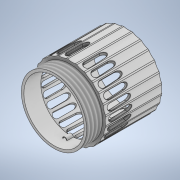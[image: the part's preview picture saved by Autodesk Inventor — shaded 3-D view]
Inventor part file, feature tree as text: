
AUTODESK INVENTOR PART (.ipt)
format: ipt  version: 2020.2 (Build 242310000, 310)  size: 1,843,200 bytes
history: native  units: mm
features: plane x14, sketch x11, extrude x9, chamfer x3, pattern_circular x3, mirror x2, emboss x1, revolve x1, split x1, thread x1, projected_geometry x1
ambient origin geometry x8: Origin, YZ Plane, XZ Plane, XY Plane, X Axis, Y Axis, Z Axis, Center Point
bodies: Solid1 (feature_tree), Solid2 (feature_tree), Solid3 (feature_tree)
feature tree (47):
  extrude  "Extrusion1"  Depth=2.0mm
  plane  "Work Plane1"
  sketch  "Sketch2"  dims[d2=4.714404mm d3=0.428883mm d4=250.0mm d6=360.0deg d8=45.0mm d9=0.0mm d11=10.0mm d12=0.0mm d15=250.0mm d16=360.0deg]
  extrude  "Extrusion2"  Depth=10.0mm
  chamfer  "Chamfer1"  Distance=250.0mm Angle=360.0deg
  chamfer  "Chamfer2"  Distance=45.0mm
  chamfer  "Chamfer3"  Distance=10.0mm
  pattern_circular  "Circular Pattern1"  Count=25 Angle=360.0deg
  plane  "Work Plane7"
  plane  "Work Plane8"
  plane  "Work Plane9"
  emboss  "Emboss1"
  revolve  "Revolution1"  Angle=45.0deg
  pattern_circular  "Circular Pattern2"  Count=4 Angle=360.0deg
  extrude  "Extrusion9"  Depth=21.5mm
  plane  "Work Plane10"
  plane  "Work Plane11"
  split  "Split1"
  extrude  "Extrusion11"  Depth=10.0mm
  thread  "Thread4"  [1 undecoded]
  plane  "Work Plane12"
  plane  "Work Plane14"
  extrude  "Extrusion12"  [1 undecoded]
  plane  "Work Plane15"
  mirror  "Mirror2"
  sketch  "Sketch21"  dims[d55=1.5mm d56=0.0mm d62=21.5mm d63=30.0mm]
  extrude  "Extrusion13"  Depth=0.5mm TaperAngle=0.0deg
  plane  "Work Plane16"
  sketch  "Sketch22"  dims[d64=0.02mm d65=1.586041mm d66=10.0mm d67=0.0mm]
  plane  "Work Plane17"
  extrude  "Extrusion14"  [1 undecoded]
  extrude  "Extrusion15"  Depth=2.878552mm
  extrude  "Extrusion16"  Depth=2.878552mm
  mirror  "Mirror3"
  pattern_circular  "Circular Pattern3"  [2 undecoded]
  sketch  "Sketch1"  dims[d0=45.0mm d1=2.0mm]
  plane  "Work Plane5"
  plane  "Work Plane6"
  sketch  "Sketch9"  dims[d18=0.9mm d19=2.0mm d20=45.0deg d21=0.9mm d22=2.0mm d23=45.0deg]
  sketch  "Sketch11"  dims[d24=0.2mm d25=2.0mm d26=45.0deg]
  sketch  "Sketch15"  dims[d37=11.75mm]
  sketch  "Sketch17"  dims[d38=-16.0mm d39=8.7mm d40=-8.7mm]
  sketch  "Sketch18"  dims[d41=0.2mm d42=0.0mm]
  plane  "Work Plane13"
  sketch  "Sketch20"  dims[d43=90.0deg d44=40.0mm d45=360.0deg]
  projected_geometry  "Projected Loop1"
  sketch  "Sketch23"  dims[d68=10.0mm d69=0.0mm d70=-2.25mm d71=0.5mm d72=0.0mm d73=-20.75mm d74=0.801779mm d75=2.939856mm d76=4.0mm d77=0.0mm d78=-1.25mm d79=2.5mm d80=0.0mm d81=1.75mm d82=0.0mm d83=2.0mm d84=0.0mm d85=20.0mm d86=360.0deg d88=2.04367mm d89=2.878552mm]
note: 5 required parameter values undecoded (feature->parameter linkage not recoverable at this tier; creation-order binding heuristic only, values carry confidence <= 0.55)
